# Revit family: NBS_ConceptCubicleSystems_PnlCbclSym_Juno
name_source: partatom
category: Specialty Equipment
units: mm (PartAtom-declared; Revit-internal decimal feet)

## family parameters
Always vertical = Yes
Cut with Voids When Loaded = No
Part Type = Normal
Room Calculation Point = No
Round Connector Dimension = Use Diameter
Shared = No
Work Plane-Based = No

## types (8) — shared parameters
Application = Junior school education sectors
AssetType = Fixed
Category = Ss_25_12_60_60:Panel cubicle systems
Color = Over 50 colour combination, contact manufacturer for details
Description = Juno washroom cubicles
DoorLeafMaterial = NBS_ConceptCubicleSystems_G029_GrisTourterelle-Grey
DurationUnit = year
Features = Black core with a radiused edge, satin anodised aluminium bolt through Ironmongery, vandel and water resistant, anti-trap hinges, shaped doors and partitions
FittingMaterial = NBS_ConceptCubicleSystems_SatinAnodisedAluminium
Fittings = Satin anodised aluminium
IfcExportAs = IfcFurnitureType
IfcExportType = USERDEFINED
IsBuiltIn = Yes
ManufacturerName = Concept Cubicle Systems
ManufacturerURL = www.conceptcubiclesystems.co.uk
Material = Compact Grade Laminate
ModelReference = Juno Washroom Cubicles
NBSCertification = www.nationalbimlibrary.com/cert/i0ywudck
NBSDescription = Panel cubicle system
NBSReference = 25-05-60/160
PanelSupports = 150 mm
PanelThickness = 13 mm
Panels = 12 mm compact grade laminate
PartitionMaterial = NBS_ConceptCubicleSystems_G029_GrisTourterelle-Grey
PilasterMaterial = NBS_ConceptCubicleSystems_G029_GrisTourterelle-Grey
ProductInformation = https://www.conceptcubiclesystems.co.uk
Size = 1500 x 1950 mm
Status = UNSET
Style = Cubicle
SystemManufacturer = Concept Cubicle Systems
Uniclass2015Code = Ss_25_12_60_60
Uniclass2015Title = Panel cubicle systems
Uniclass2015Version = Systems v1.17
Version = 3
WarrantyDurationUnit = year

## per-type parameters (varying)
| type | BIMObjectName | HasFittingsLeft | HasFittingsRight | HasPartitionLeft | HasPartitionRight | HasPilasterPanelReturnLeft | HasPilasterPanelReturnRight | IsEndCubicle | IsFirstCubicle | IsMiddleCubicle | IsSingleCubicle | IsWallEndEndCubicle | IsWallEndFirstCubicle | IsWallEndSingleCubicle | IsWallToWallSingleCubicle | Name | PilasterPanelReturnLeft | PilasterPanelReturnRight |
| SingleCubicle | NBS_ConceptCubicleSystems_PanelCubicleSystem_Juno_SingleCubicle | No | No | Yes | Yes | Yes | Yes | No | No | No | Yes | No | No | No | No | PanelCubicleSystem_Juno_SingleCubicle_ConceptCubicleSystems | 6 mm  [stored 0.019685 ft] | 6 mm  [stored 0.019685 ft] |
| WallToWallSingleCubicle | NBS_ConceptCubicleSystems_PanelCubicleSystem_Juno_WallToWallSingleCubicle | Yes | Yes | No | No | No | No | No | No | No | No | No | No | No | Yes | PanelCubicleSystem_Juno_WallToWallSingleCubicle_ConceptCubicleSystems | 0 mm  [stored 0 ft] | 0 mm  [stored 0 ft] |
| EndCubicle | NBS_ConceptCubicleSystems_PanelCubicleSystem_Juno_EndCubicle | No | No | No | Yes | No | Yes | Yes | No | No | No | No | No | No | No | PanelCubicleSystem_Juno_EndCubicle_ConceptCubicleSystems | 0 mm  [stored 0 ft] | 6 mm  [stored 0.019685 ft] |
| FirstCubicle | NBS_ConceptCubicleSystems_PanelCubicleSystem_Juno_FirstCubicle | No | No | Yes | Yes | Yes | No | No | Yes | No | No | No | No | No | No | PanelCubicleSystem_Juno_FirstCubicle_ConceptCubicleSystems | 6 mm  [stored 0.019685 ft] | 0 mm  [stored 0 ft] |
| WallEndFirstCubicle | NBS_ConceptCubicleSystems_PanelCubicleSystem_Juno_WallEndFirstCubicle | Yes | No | No | Yes | No | No | No | No | No | No | No | Yes | No | No | PanelCubicleSystem_Juno_WallEndFirstCubicle_ConceptCubicleSystems | 0 mm  [stored 0 ft] | 0 mm  [stored 0 ft] |
| WallEndSingleCubicle | NBS_ConceptCubicleSystems_PanelCubicleSystem_Juno_WallEndSingleCubicle | Yes | No | No | Yes | No | Yes | No | No | No | No | No | No | Yes | No | PanelCubicleSystem_Juno_WallEndSingleCubicle_ConceptCubicleSystems | 0 mm  [stored 0 ft] | 6 mm  [stored 0.019685 ft] |
| MiddleCubicle | NBS_ConceptCubicleSystems_PanelCubicleSystem_Juno_MiddleCubicle | No | No | No | Yes | No | No | No | No | Yes | No | No | No | No | No | PanelCubicleSystem_Juno_MiddleCubicle_ConceptCubicleSystems | 0 mm  [stored 0 ft] | 0 mm  [stored 0 ft] |
| WallEndEndCubicle | NBS_ConceptCubicleSystems_PanelCubicleSystem_Juno_WallEndEndCubicle | No | Yes | No | No | No | No | No | No | No | No | Yes | No | No | No | PanelCubicleSystem_Juno_WallEndEndCubicle_ConceptCubicleSystems | 0 mm  [stored 0 ft] | 0 mm  [stored 0 ft] |

note: [stored X ft] marks values corroborated as IEEE doubles in the binary element streams (Revit-internal decimal feet)

## geometry (parser evidence)
native form markers: Sweep x7
no freeform markers — native parametric forms only
